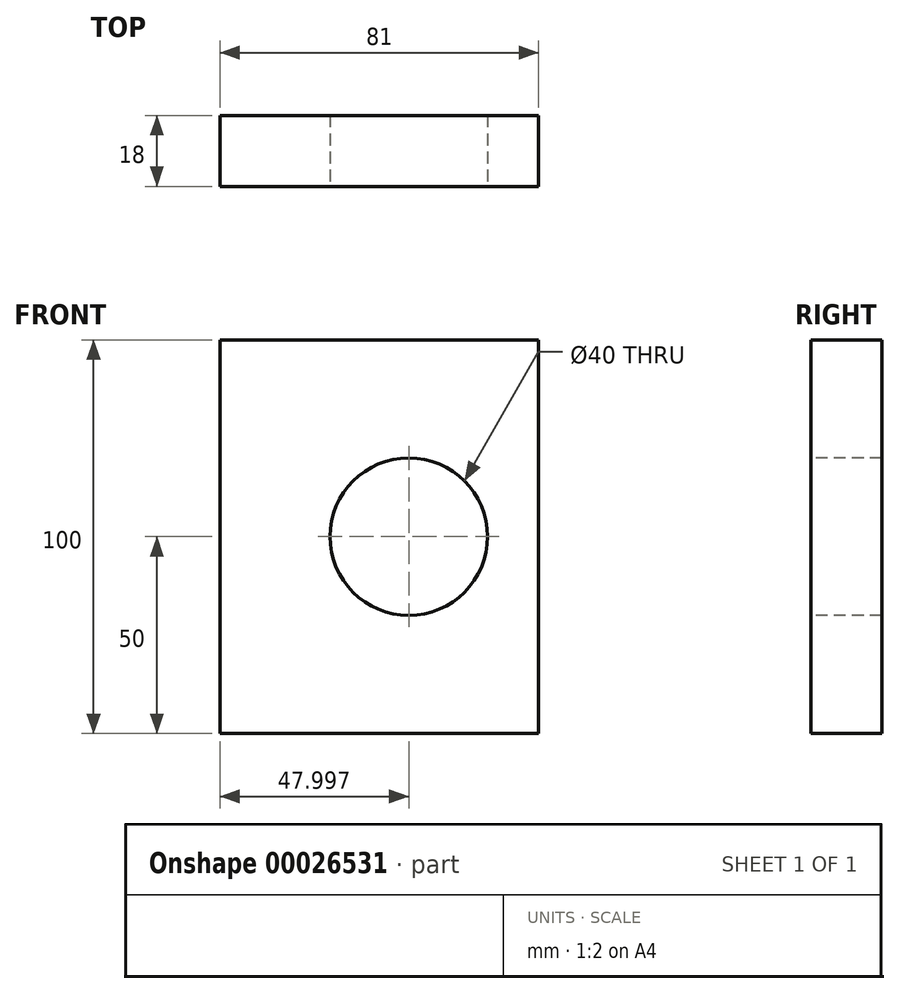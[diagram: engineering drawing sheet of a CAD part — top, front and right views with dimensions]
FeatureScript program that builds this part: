
annotation { "Feature Type Name" : "Feature", "Feature Type Description" : "" }
export const myFeature = defineFeature(function(context is Context, id is Id, definition is map)
    precondition{}
    {
        {
            var Q0;
            Q0=qCreatedBy(makeId("Top.planeOp"),FACE);
            var sketch = newSketch(context, id + "F0", { "sketchPlane" : qUnion([Q0])});
            skArc(sketch, "E0", {"start": v(34.96, 91.8) * mm, "mid": v(-134.14, 76.3) * mm, "end": v(-20.7, -50.05) * mm});
            skArc(sketch, "E1", {"start": v(54.3, 41.6) * mm, "mid": v(-129.12, 96.76) * mm, "end": v(-6.54, -50.41) * mm});
            skLineSegment(sketch, "E2", {"start": v(57.3, 41.6) * mm, "end": v(57.3, -83.4) * mm});
            skLineSegment(sketch, "E3", {"start": v(54.3, 41.6) * mm, "end": v(54.3, -65.4) * mm});
            skLineSegment(sketch, "E4", {"start": v(-23.7, -59.02) * mm, "end": v(-23.7, -83.4) * mm});
            skLineSegment(sketch, "E5", {"start": v(57.3, -65.4) * mm, "end": v(-23.7, -65.4) * mm});
            skLineSegment(sketch, "E6", {"start": v(79.3, 41.6) * mm, "end": v(79.19, -83.4) * mm});
            skLineSegment(sketch, "E7", {"start": v(-12.85, -33.67) * mm, "end": v(-13.26, -32.74) * mm});
            skLineSegment(sketch, "E8", {"start": v(28.64, 74.05) * mm, "end": v(29.57, 74.45) * mm});
            skArc(sketch, "E9", {"start": v(13.66, 78.69) * mm, "mid": v(-110.87, 67.17) * mm, "end": v(-27.4, -25.96) * mm});
            skPoint(sketch, "E10.visualSharp", {"position": v(41.37, 79.6) * mm});
            skArc(sketch, "E10.filletArc", {"start": v(29.57, 74.45) * mm, "mid": v(36.23, 81.9) * mm, "end": v(34.96, 91.8) * mm});
            skPoint(sketch, "E11.visualSharp", {"position": v(18.45, 69.6) * mm});
            skArc(sketch, "E11.filletArc", {"start": v(13.66, 78.69) * mm, "mid": v(20.3, 73.59) * mm, "end": v(28.64, 74.05) * mm});
            skPoint(sketch, "E12.visualSharp", {"position": v(-17.7, -22.55) * mm});
            skArc(sketch, "E12.filletArc", {"start": v(-13.26, -32.74) * mm, "mid": v(-19.06, -26.72) * mm, "end": v(-27.4, -25.96) * mm});
            skPoint(sketch, "E13.visualSharp", {"position": v(-7.7, -45.47) * mm});
            skArc(sketch, "E13.filletArc", {"start": v(-20.7, -50.05) * mm, "mid": v(-13.03, -43.65) * mm, "end": v(-12.85, -33.67) * mm});
            skLineSegment(sketch, "E14", {"start": v(-5.7, -53.31) * mm, "end": v(-6.54, -50.41) * mm});
            skArc(sketch, "E15", {"start": v(79.3, 41.38) * mm, "mid": v(-134.01, 130.07) * mm, "end": v(-45.7, -83.4) * mm});
            skLineSegment(sketch, "E16", {"start": v(-45.7, -83.4) * mm, "end": v(-23.7, -83.4) * mm});
            skLineSegment(sketch, "E17", {"start": v(-23.7, -83.4) * mm, "end": v(79.19, -83.4) * mm});
            skLineSegment(sketch, "E18", {"start": v(54.3, -47.4) * mm, "end": v(6.14, -47.4) * mm});
            skCircle(sketch, "E19", {"center": v(-45.7, 41.6) * mm, "radius": 103 * mm});
            skSolve(sketch);
        }
        {
            var Q0;
            {var subQ0=sQuery(id+"F0.wireOp",EDGE,"E17");var subQ3=sQuery(id+"F0.wireOp",EDGE,"E2");var subQ4=makeQuery(id+"F0.imprint","INTERSECT",VERTEX,{"derivedFrom":[subQ3,subQ0]});Q0=makeQuery(id+"F0.imprint","IMPRINT",FACE,{"disambiguationData":[TD([[makeQuery(id+"F0.imprint","IMPRINT",EDGE,{"disambiguationData":[TD([[subQ4,1.0]])],"derivedFrom":subQ3}),-1.0]])]});}
            extrude(context, id + "F1", {"entities" : qUnion([Q0]), "depth" : 100 * mm});
        }
        {
            var Q0;
            Q0=makeQuery(id+"F1.opExtrude","SWEPT_FACE",FACE,{"disambiguationData":[OSD([sQuery(id+"F0.wireOp",EDGE,"E17")])]});
            var sketch = newSketch(context, id + "F2", { "sketchPlane" : qUnion([Q0])});
            skCircle(sketch, "E20", {"center": v(24.3, 50) * mm, "radius": 20 * mm});
            skSolve(sketch);
        }
        {
            var Q0;
            Q0=makeQuery(id+"F2.imprint","IMPRINT",FACE,{"disambiguationData":[TD([[makeQuery(id+"F2.imprint","IMPRINT",EDGE,{"derivedFrom":sQuery(id+"F2.wireOp",EDGE,"E20")}),1.0]])]});
            extrude(context, id + "F3", {"entities" : qUnion([Q0]), "operationType" : NewBodyOperationType.REMOVE, "oppositeDirection" : true, "depth" : 25 * mm});
        }
    });
